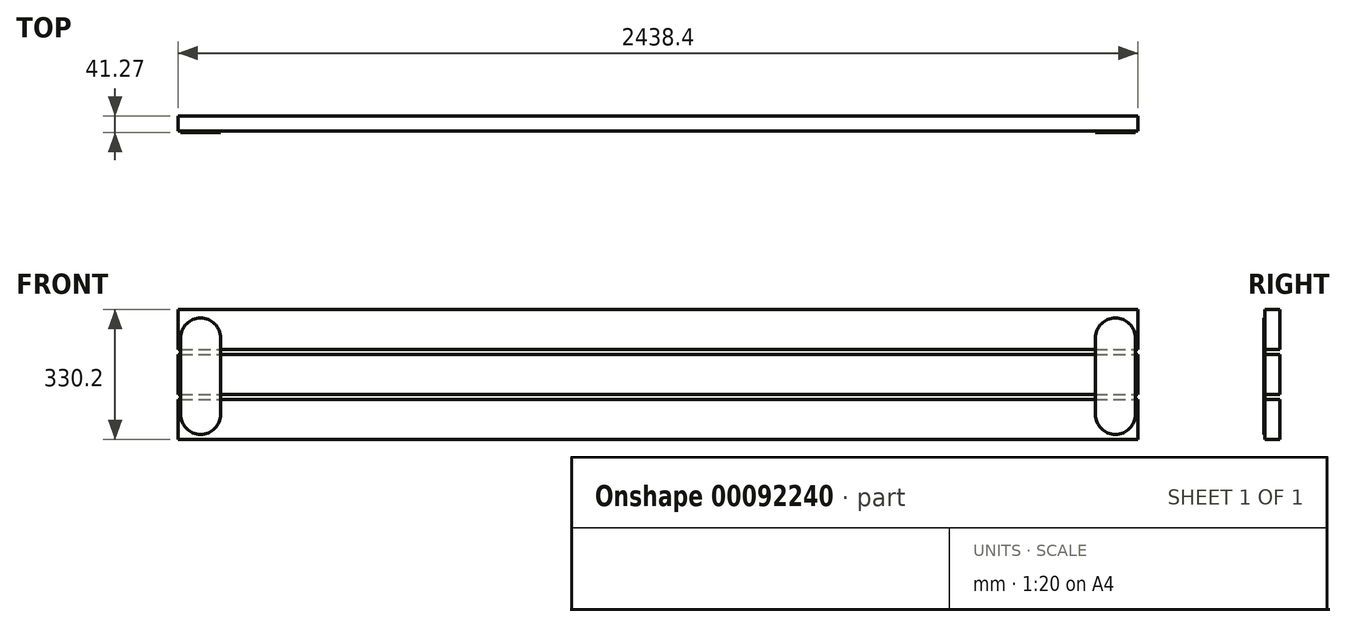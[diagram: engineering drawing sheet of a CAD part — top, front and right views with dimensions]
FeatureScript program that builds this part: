
annotation { "Feature Type Name" : "Feature", "Feature Type Description" : "" }
export const myFeature = defineFeature(function(context is Context, id is Id, definition is map)
    precondition{}
    {
        {
            var Q0;
            Q0=qCreatedBy(makeId("Front.planeOp"),FACE);
            var sketch = newSketch(context, id + "F0", { "sketchPlane" : qUnion([Q0])});
            skLineSegment(sketch, "E0.bottom", {"start": v(-1219.2, 114.3) * mm, "end": v(1219.2, 114.3) * mm});
            skLineSegment(sketch, "E0.top", {"start": v(-1219.2, 12.7) * mm, "end": v(1219.2, 12.7) * mm});
            skLineSegment(sketch, "E0.left", {"start": v(-1219.2, 114.3) * mm, "end": v(-1219.2, 12.7) * mm});
            skLineSegment(sketch, "E0.right", {"start": v(1219.2, 114.3) * mm, "end": v(1219.2, 12.7) * mm});
            skLineSegment(sketch, "E1.bottom", {"start": v(-1219.2, 0) * mm, "end": v(1219.2, 0) * mm});
            skLineSegment(sketch, "E1.top", {"start": v(-1219.2, -101.6) * mm, "end": v(1219.2, -101.6) * mm});
            skLineSegment(sketch, "E1.left", {"start": v(-1219.2, 0) * mm, "end": v(-1219.2, -101.6) * mm});
            skLineSegment(sketch, "E1.right", {"start": v(1219.2, 0) * mm, "end": v(1219.2, -101.6) * mm});
            skLineSegment(sketch, "E2.bottom", {"start": v(-1219.2, -114.3) * mm, "end": v(1219.2, -114.3) * mm});
            skLineSegment(sketch, "E2.top", {"start": v(-1219.2, -215.9) * mm, "end": v(1219.2, -215.9) * mm});
            skLineSegment(sketch, "E2.left", {"start": v(-1219.2, -114.3) * mm, "end": v(-1219.2, -215.9) * mm});
            skLineSegment(sketch, "E2.right", {"start": v(1219.2, -114.3) * mm, "end": v(1219.2, -215.9) * mm});
            skSolve(sketch);
        }
        {
            var Q0;
            Q0 = qSketchRegion(id + "F0", true);
            extrude(context, id + "F1", {"entities" : qUnion([Q0]), "depth" : 38.1 * mm});
        }
        {
            var Q0;
            Q0=makeQuery(id+"F1.opExtrude","CAP_FACE",FACE,{"disambiguationData":[OSD([sQuery(id+"F0.wireOp",EDGE,"E0.bottom"),sQuery(id+"F0.wireOp",EDGE,"E0.top"),sQuery(id+"F0.wireOp",EDGE,"E0.left"),sQuery(id+"F0.wireOp",EDGE,"E0.right")])],"isStart":false});
            var sketch = newSketch(context, id + "F2", { "sketchPlane" : qUnion([Q0])});
            skLineSegment(sketch, "E3.left", {"start": v(-1212.85, -152.4) * mm, "end": v(-1212.85, 41.94) * mm});
            skLineSegment(sketch, "E3.right", {"start": v(-1111.25, -152.4) * mm, "end": v(-1111.25, 41.94) * mm});
            skLineSegment(sketch, "E4.left", {"start": v(1111.25, -152.4) * mm, "end": v(1111.25, 41.94) * mm});
            skLineSegment(sketch, "E4.right", {"start": v(1212.85, -152.4) * mm, "end": v(1212.85, 41.94) * mm});
            skArc(sketch, "E5", {"start": v(1212.85, 41.94) * mm, "mid": v(1162.05, 92.74) * mm, "end": v(1111.25, 41.94) * mm});
            skArc(sketch, "E6", {"start": v(1111.25, -152.4) * mm, "mid": v(1162.05, -203.2) * mm, "end": v(1212.85, -152.4) * mm});
            skArc(sketch, "E7", {"start": v(-1111.25, 41.94) * mm, "mid": v(-1162.05, 92.74) * mm, "end": v(-1212.85, 41.94) * mm});
            skArc(sketch, "E8", {"start": v(-1212.85, -152.4) * mm, "mid": v(-1162.05, -203.2) * mm, "end": v(-1111.25, -152.4) * mm});
            skSolve(sketch);
        }
        {
            var Q0;
            Q0 = qSketchRegion(id + "F2", true);
            extrude(context, id + "F3", {"entities" : qUnion([Q0]), "depth" : 3.17 * mm});
        }
    });
